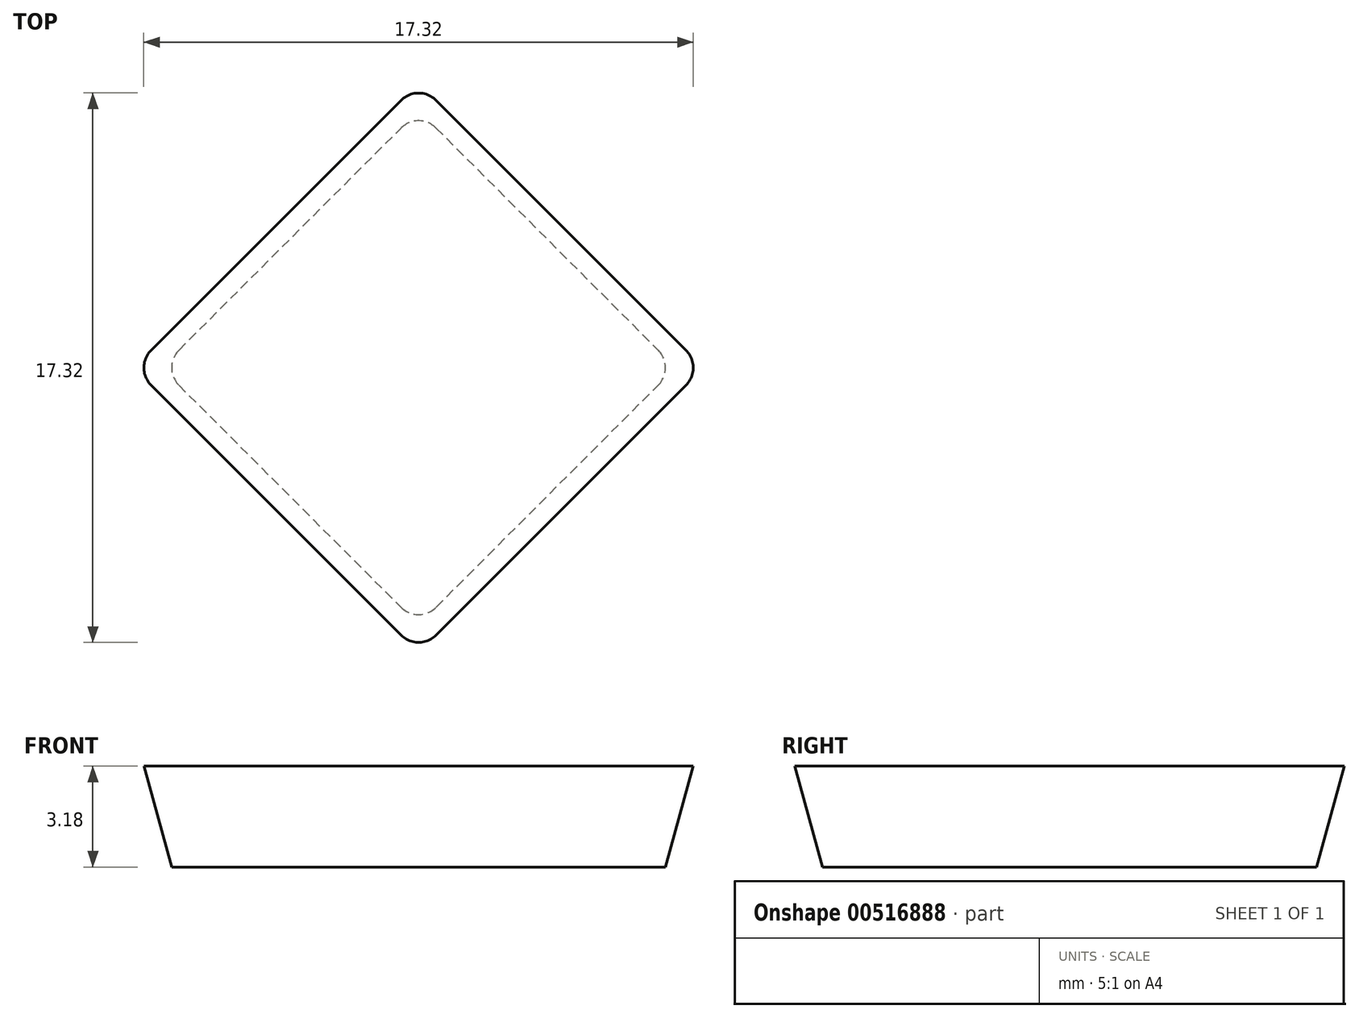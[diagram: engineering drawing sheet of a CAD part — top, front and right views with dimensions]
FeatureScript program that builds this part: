
annotation { "Feature Type Name" : "Feature", "Feature Type Description" : "" }
export const myFeature = defineFeature(function(context is Context, id is Id, definition is map)
    precondition{}
    {
        {
            var Q0;
            Q0=qCreatedBy(makeId("Top.planeOp"),FACE);
            var sketch = newSketch(context, id + "F0", { "sketchPlane" : qUnion([Q0])});
            skLineSegment(sketch, "E0.bottom", {"start": v(6.35, 6.35) * mm, "end": v(-6.35, 6.35) * mm});
            skLineSegment(sketch, "E0.top", {"start": v(6.35, -6.35) * mm, "end": v(-6.35, -6.35) * mm});
            skLineSegment(sketch, "E0.left", {"start": v(6.35, 6.35) * mm, "end": v(6.35, -6.35) * mm});
            skLineSegment(sketch, "E0.right", {"start": v(-6.35, 6.35) * mm, "end": v(-6.35, -6.35) * mm});
            skPoint(sketch, "E0.middle", {"position": v(0, 0) * mm});
            skSolve(sketch);
        }
        {
            var Q0;
            Q0 = qSketchRegion(id + "F0", true);
            extrude(context, id + "F1", {"entities" : qUnion([Q0]), "depth" : 3.18 * mm, "offsetDistance" : 25 * mm});
        }
        {
            var Q0;
            Q0=makeQuery(id+"F1.opExtrude","SWEPT_FACE",FACE,{"disambiguationData":[OSD([sQuery(id+"F0.wireOp",EDGE,"E0.top")])]});
            var sketch = newSketch(context, id + "F2", { "sketchPlane" : qUnion([Q0])});
            skLineSegment(sketch, "E1.0", {"start": v(6.35, 3.18) * mm, "end": v(-6.35, 3.18) * mm});
            skLineSegment(sketch, "E2.0", {"start": v(5.73, 0) * mm, "end": v(-5.73, 0) * mm});
            skLineSegment(sketch, "E3", {"start": v(6.35, 3.18) * mm, "end": v(5.73, 0) * mm});
            skLineSegment(sketch, "E4", {"start": v(0, 0) * mm, "end": v(0, 1.4) * mm, "construction": true});
            skPoint(sketch, "E4.endSnap0", {"position": v(0, 0) * mm});
            skLineSegment(sketch, "E5.MirrorCS", {"start": v(-6.35, 3.18) * mm, "end": v(-5.73, 0) * mm});
            skPoint(sketch, "E6.orphan", {"position": v(6.35, 0) * mm});
            skPoint(sketch, "E7.orphan", {"position": v(-6.35, 0) * mm});
            skSolve(sketch);
        }
        {
            var Q0;
            {var subQ0=sQuery(id+"F2.wireOp",EDGE,"E3");Q0=makeQuery(id+"F2.imprint","IMPRINT",FACE,{"disambiguationData":[TD([[makeQuery(id+"F2.imprint","IMPRINT",EDGE,{"derivedFrom":subQ0}),1.0]])]});}
            var Q1;
            {var subQ0=sQuery(id+"F2.wireOp",EDGE,"E5.MirrorCS");Q1=makeQuery(id+"F2.imprint","IMPRINT",FACE,{"disambiguationData":[TD([[makeQuery(id+"F2.imprint","IMPRINT",EDGE,{"derivedFrom":subQ0}),-1.0]])]});}
            extrude(context, id + "F3", {"entities" : qUnion([Q0, Q1]), "operationType" : NewBodyOperationType.REMOVE, "endBound" : BoundingType.THROUGH_ALL, "oppositeDirection" : true, "depth" : 25 * mm, "offsetDistance" : 25 * mm});
        }
        {
            var Q0;
            Q0=qCreatedBy(makeId("Right.planeOp"),FACE);
            var sketch = newSketch(context, id + "F4", { "sketchPlane" : qUnion([Q0])});
            skLineSegment(sketch, "E8.0.0", {"start": v(6.35, 3.18) * mm, "end": v(-6.35, 3.18) * mm});
            skLineSegment(sketch, "E8.0.1", {"start": v(-6.35, 3.18) * mm, "end": v(-6.35, 0) * mm});
            skLineSegment(sketch, "E8.0.2", {"start": v(-6.35, 0) * mm, "end": v(6.35, 0) * mm});
            skLineSegment(sketch, "E8.0.3", {"start": v(6.35, 0) * mm, "end": v(6.35, 3.18) * mm});
            skLineSegment(sketch, "E9", {"start": v(-6.35, 3.18) * mm, "end": v(-5.73, 0) * mm});
            skLineSegment(sketch, "E10", {"start": v(0, 0) * mm, "end": v(0, 1.4) * mm, "construction": true});
            skLineSegment(sketch, "E11.MirrorCS", {"start": v(6.35, 3.18) * mm, "end": v(5.73, 0) * mm});
            skSolve(sketch);
        }
        {
            var Q0;
            {var subQ0=sQuery(id+"F4.wireOp",EDGE,"E8.0.3");Q0=makeQuery(id+"F4.imprint","IMPRINT",FACE,{"disambiguationData":[TD([[makeQuery(id+"F4.imprint","IMPRINT",EDGE,{"derivedFrom":subQ0}),1.0]])]});}
            var Q1;
            {var subQ0=sQuery(id+"F4.wireOp",EDGE,"E8.0.1");Q1=makeQuery(id+"F4.imprint","IMPRINT",FACE,{"disambiguationData":[TD([[makeQuery(id+"F4.imprint","IMPRINT",EDGE,{"derivedFrom":subQ0}),1.0]])]});}
            extrude(context, id + "F5", {"entities" : qUnion([Q0, Q1]), "operationType" : NewBodyOperationType.REMOVE, "oppositeDirection" : true, "depth" : 13 * mm, "offsetDistance" : 25 * mm, "symmetric" : true});
        }
        {
            var Q0;
            Q0=makeQuery(id+"F5.boolean.opBoolean","INTERSECT",EDGE,{"derivedFrom":[makeQuery(id+"F3.boolean.opBoolean","COPY",FACE,{"derivedFrom":makeQuery(id+"F3.opExtrude","SWEPT_FACE",FACE,{"disambiguationData":[OSD([sQuery(id+"F2.wireOp",EDGE,"E3")])]})}),makeQuery(id+"F5.opExtrude","SWEPT_FACE",FACE,{"disambiguationData":[OSD([sQuery(id+"F4.wireOp",EDGE,"E9")])]})]});
            var Q1;
            Q1=makeQuery(id+"F5.boolean.opBoolean","INTERSECT",EDGE,{"derivedFrom":[makeQuery(id+"F3.boolean.opBoolean","COPY",FACE,{"derivedFrom":makeQuery(id+"F3.opExtrude","SWEPT_FACE",FACE,{"disambiguationData":[OSD([sQuery(id+"F2.wireOp",EDGE,"E5.MirrorCS")])]})}),makeQuery(id+"F5.opExtrude","SWEPT_FACE",FACE,{"disambiguationData":[OSD([sQuery(id+"F4.wireOp",EDGE,"E9")])]})]});
            var Q2;
            Q2=makeQuery(id+"F5.boolean.opBoolean","INTERSECT",EDGE,{"derivedFrom":[makeQuery(id+"F3.boolean.opBoolean","COPY",FACE,{"derivedFrom":makeQuery(id+"F3.opExtrude","SWEPT_FACE",FACE,{"disambiguationData":[OSD([sQuery(id+"F2.wireOp",EDGE,"E3")])]})}),makeQuery(id+"F5.opExtrude","SWEPT_FACE",FACE,{"disambiguationData":[OSD([sQuery(id+"F4.wireOp",EDGE,"E11.MirrorCS")])]})]});
            var Q3;
            Q3=makeQuery(id+"F5.boolean.opBoolean","INTERSECT",EDGE,{"derivedFrom":[makeQuery(id+"F3.boolean.opBoolean","COPY",FACE,{"derivedFrom":makeQuery(id+"F3.opExtrude","SWEPT_FACE",FACE,{"disambiguationData":[OSD([sQuery(id+"F2.wireOp",EDGE,"E5.MirrorCS")])]})}),makeQuery(id+"F5.opExtrude","SWEPT_FACE",FACE,{"disambiguationData":[OSD([sQuery(id+"F4.wireOp",EDGE,"E11.MirrorCS")])]})]});
            fillet(context, id + "F6", {"entities" : qUnion([Q0, Q1, Q2, Q3]), "radius" : 0.8 * mm, "tangentPropagation" : true, "allowEdgeOverflow" : false});
        }
        {
            var Q0;
            Q0=makeQuery(id+"F1.opExtrude","SWEPT_BODY",BODY,{"disambiguationData":[OSD([sQuery(id+"F0.wireOp",EDGE,"E0.bottom"),sQuery(id+"F0.wireOp",EDGE,"E0.top"),sQuery(id+"F0.wireOp",EDGE,"E0.left"),sQuery(id+"F0.wireOp",EDGE,"E0.right")])]});
            var Q1;
            Q1=sQuery(id+"F4.wireOp",EDGE,"E10");
            transform(context, id + "F7", {"entities" : qUnion([Q0]), "transformType" : TransformType.ROTATION, "transformAxis" : qUnion([Q1]), "angle" : 45 * degree, "makeCopy" : false});
        }
    });
